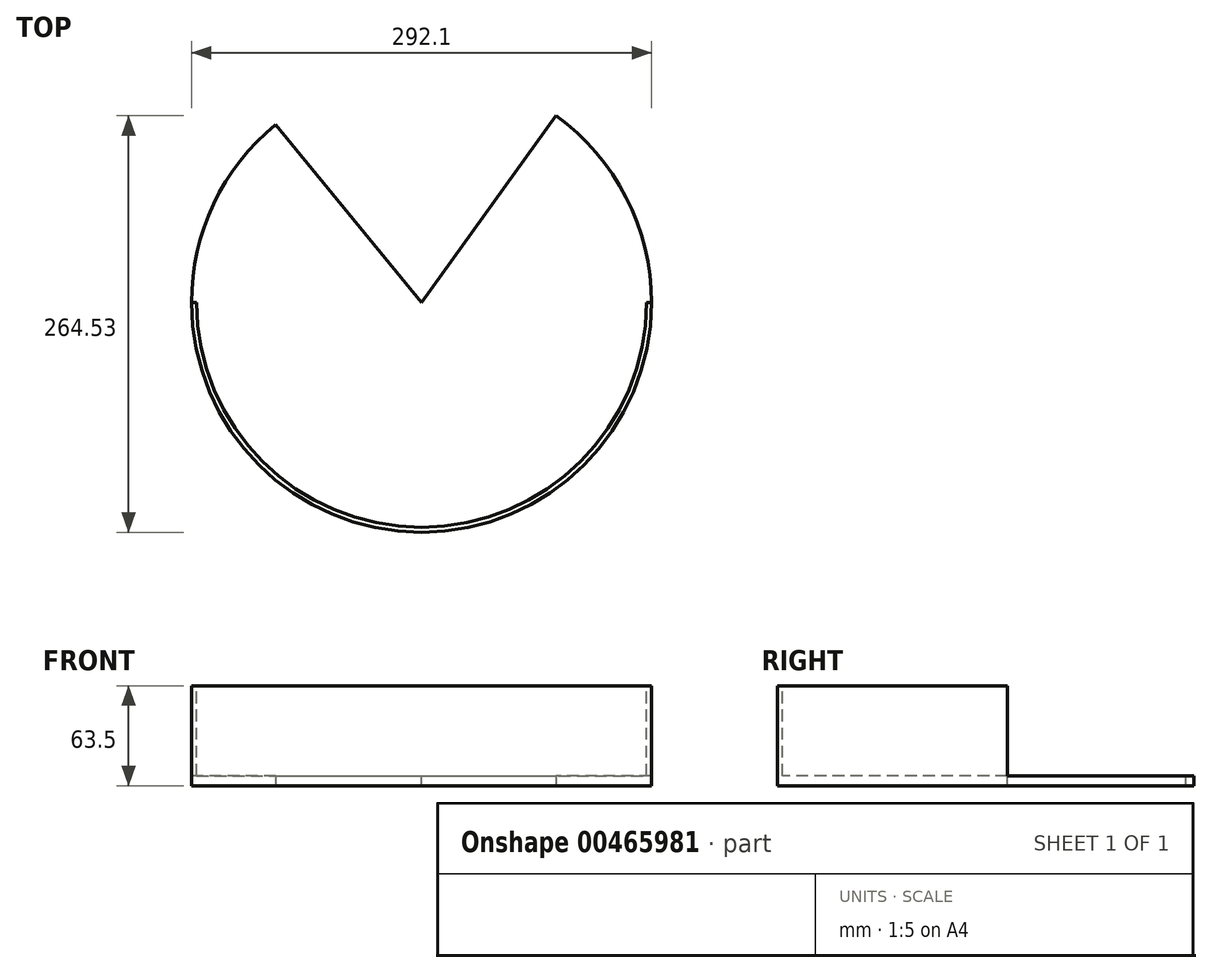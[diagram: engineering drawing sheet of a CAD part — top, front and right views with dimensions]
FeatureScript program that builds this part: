
annotation { "Feature Type Name" : "Feature", "Feature Type Description" : "" }
export const myFeature = defineFeature(function(context is Context, id is Id, definition is map)
    precondition{}
    {
        {
            var Q0;
            Q0=qCreatedBy(makeId("Top.planeOp"),FACE);
            var sketch = newSketch(context, id + "F0", { "sketchPlane" : qUnion([Q0])});
            skCircle(sketch, "E0", {"center": v(0, 0) * mm, "radius": 146.05 * mm});
            skSolve(sketch);
        }
        {
            var Q0;
            Q0=makeQuery(id+"F0.imprint","IMPRINT",FACE,{"disambiguationData":[TD([[makeQuery(id+"F0.imprint","IMPRINT",EDGE,{"derivedFrom":sQuery(id+"F0.wireOp",EDGE,"E0")}),1.0]])]});
            extrude(context, id + "F1", {"entities" : qUnion([Q0]), "depth" : 63.5 * mm});
        }
        {
            var Q0;
            Q0=makeQuery(id+"F1.opExtrude","CAP_FACE",FACE,{"disambiguationData":[OSD([sQuery(id+"F0.wireOp",EDGE,"E0")])],"isStart":false});
            var sketch = newSketch(context, id + "F2", { "sketchPlane" : qUnion([Q0])});
            skCircle(sketch, "E1", {"center": v(0, 0) * mm, "radius": 142.88 * mm});
            skSolve(sketch);
        }
        {
            var Q0;
            Q0=makeQuery(id+"F2.imprint","IMPRINT",FACE,{"disambiguationData":[TD([[makeQuery(id+"F2.imprint","IMPRINT",EDGE,{"derivedFrom":sQuery(id+"F2.wireOp",EDGE,"E1")}),1.0]])]});
            extrude(context, id + "F3", {"entities" : qUnion([Q0]), "operationType" : NewBodyOperationType.REMOVE, "depth" : -57.15 * mm});
        }
        {
            var Q0;
            Q0=makeQuery(id+"F2.imprint","IMPRINT",FACE,{"disambiguationData":[TD([[makeQuery(id+"F2.imprint","IMPRINT",EDGE,{"derivedFrom":sQuery(id+"F2.wireOp",EDGE,"E1")}),1.0]])]});
            var sketch = newSketch(context, id + "F4", { "sketchPlane" : qUnion([Q0])});
            skLineSegment(sketch, "E2.bottom", {"start": v(186.45, 0) * mm, "end": v(-190.86, 0) * mm});
            skLineSegment(sketch, "E2.top", {"start": v(186.45, 147.84) * mm, "end": v(-190.86, 147.84) * mm});
            skLineSegment(sketch, "E2.left", {"start": v(186.45, 0) * mm, "end": v(186.45, 147.84) * mm});
            skLineSegment(sketch, "E2.right", {"start": v(-190.86, 0) * mm, "end": v(-190.86, 147.84) * mm});
            skSolve(sketch);
        }
        {
            var Q0;
            Q0=makeQuery(id+"F4.imprint","IMPRINT",FACE,{"disambiguationData":[TD([[makeQuery(id+"F4.imprint","IMPRINT",EDGE,{"derivedFrom":sQuery(id+"F4.wireOp",EDGE,"E2.top")}),1.0]])]});
            extrude(context, id + "F5", {"entities" : qUnion([Q0]), "operationType" : NewBodyOperationType.REMOVE, "oppositeDirection" : true, "depth" : 57.15 * mm});
        }
        {
            var Q0;
            Q0=makeQuery(id+"F2.imprint","IMPRINT",FACE,{"disambiguationData":[TD([[makeQuery(id+"F2.imprint","IMPRINT",EDGE,{"derivedFrom":sQuery(id+"F2.wireOp",EDGE,"E1")}),1.0]])]});
            var sketch = newSketch(context, id + "F6", { "sketchPlane" : qUnion([Q0])});
            skArc(sketch, "E3", {"start": v(92.83, 128.78) * mm, "mid": v(-4.76, 152.33) * mm, "end": v(-100.68, 122.74) * mm});
            skLineSegment(sketch, "E4", {"start": v(0, 0) * mm, "end": v(92.83, 128.78) * mm});
            skLineSegment(sketch, "E5", {"start": v(-100.68, 122.74) * mm, "end": v(0, 0) * mm});
            skSolve(sketch);
        }
        {
            var Q0;
            Q0 = qSketchRegion(id + "F6", true);
            extrude(context, id + "F7", {"entities" : qUnion([Q0]), "operationType" : NewBodyOperationType.REMOVE, "endBound" : BoundingType.THROUGH_ALL, "oppositeDirection" : true, "depth" : 25.4 * mm});
        }
    });
